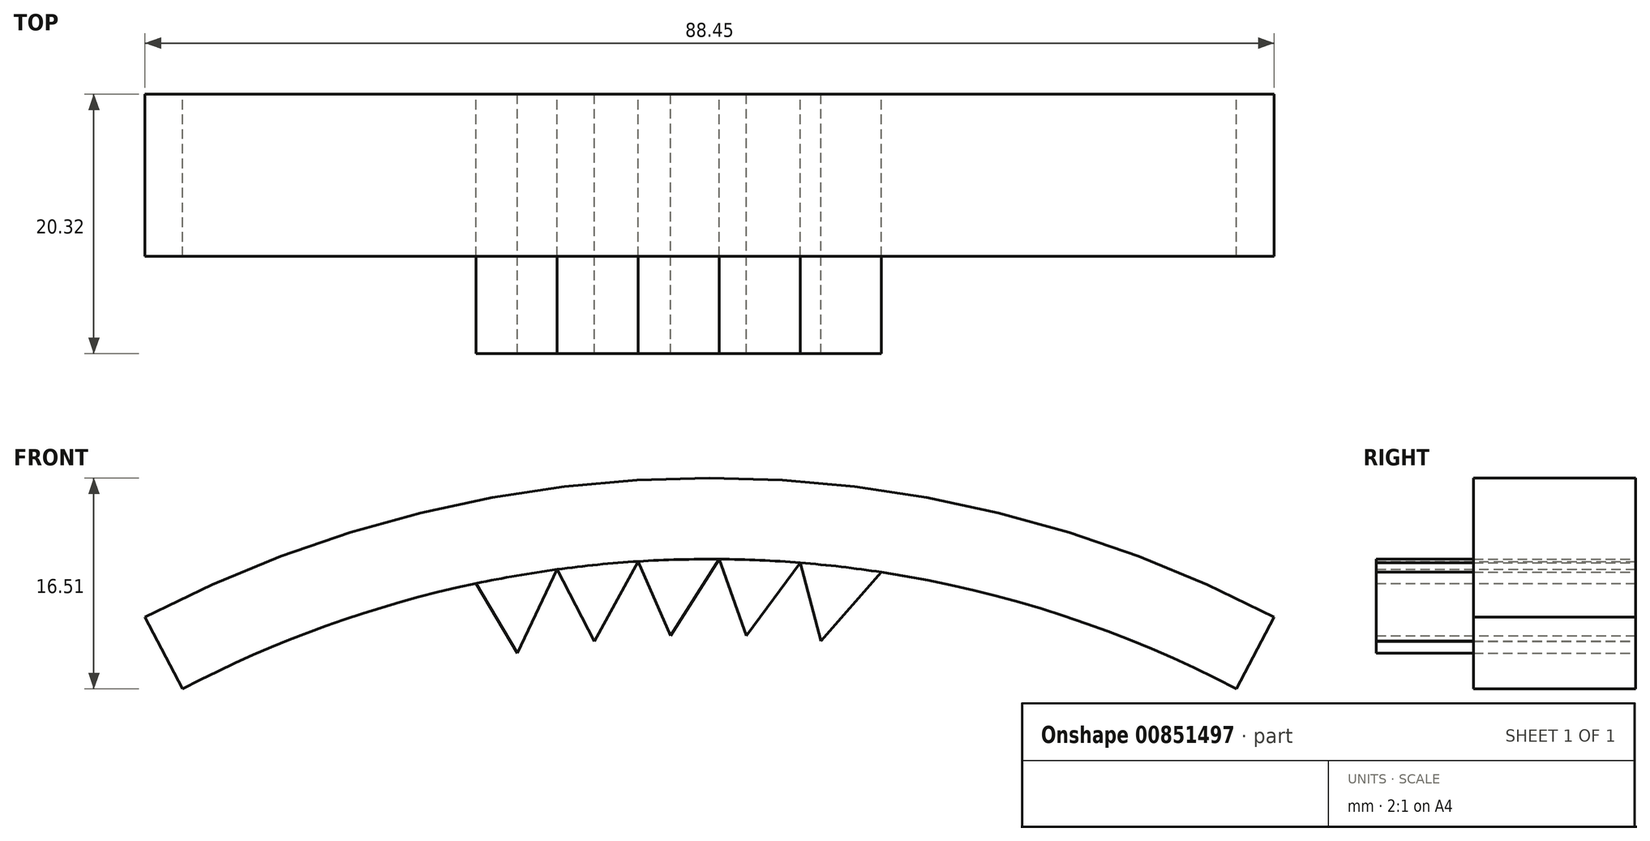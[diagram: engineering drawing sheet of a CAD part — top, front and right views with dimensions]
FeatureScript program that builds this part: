
annotation { "Feature Type Name" : "Feature", "Feature Type Description" : "" }
export const myFeature = defineFeature(function(context is Context, id is Id, definition is map)
    precondition{}
    {
        {
            var Q0;
            Q0=qCreatedBy(makeId("Front.planeOp"),FACE);
            var sketch = newSketch(context, id + "F0", { "sketchPlane" : qUnion([Q0])});
            skLineSegment(sketch, "E0", {"start": v(0, 0) * mm, "end": v(82.55, 0) * mm});
            skArc(sketch, "E1", {"start": v(82.55, 0) * mm, "mid": v(41.28, 10.16) * mm, "end": v(0, 0) * mm});
            skArc(sketch, "E2.0", {"start": v(85.5, 5.62) * mm, "mid": v(41.28, 16.51) * mm, "end": v(-2.95, 5.62) * mm});
            skLineSegment(sketch, "E3", {"start": v(0, 0) * mm, "end": v(-2.95, 5.62) * mm});
            skLineSegment(sketch, "E4", {"start": v(82.55, 0) * mm, "end": v(85.5, 5.62) * mm});
            skSolve(sketch);
        }
        {
            var Q0;
            Q0=makeQuery(id+"F0.imprint","IMPRINT",FACE,{"disambiguationData":[TD([[makeQuery(id+"F0.imprint","IMPRINT",EDGE,{"derivedFrom":sQuery(id+"F0.wireOp",EDGE,"E1")}),-1.0]])]});
            extrude(context, id + "F1", {"entities" : qUnion([Q0]), "depth" : 12.7 * mm, "offsetDistance" : 25.4 * mm});
        }
        {
            var Q0;
            Q0=makeQuery(id+"F1.opExtrude","CAP_FACE",FACE,{"disambiguationData":[OSD([sQuery(id+"F0.wireOp",EDGE,"E1"),sQuery(id+"F0.wireOp",EDGE,"E2.0"),sQuery(id+"F0.wireOp",EDGE,"E3"),sQuery(id+"F0.wireOp",EDGE,"E4")])],"isStart":false});
            var sketch = newSketch(context, id + "F2", { "sketchPlane" : qUnion([Q0])});
            skLineSegment(sketch, "E5", {"start": v(10.3, 4.59) * mm, "end": v(15.43, -0.34) * mm});
            skLineSegment(sketch, "E6", {"start": v(15.43, -0.34) * mm, "end": v(16.64, 6.68) * mm});
            skLineSegment(sketch, "E7", {"start": v(16.64, 6.68) * mm, "end": v(20.15, 1.39) * mm});
            skLineSegment(sketch, "E8", {"start": v(20.15, 1.39) * mm, "end": v(23, 8.26) * mm});
            skLineSegment(sketch, "E9", {"start": v(23, 8.26) * mm, "end": v(26.22, 2.8) * mm});
            skLineSegment(sketch, "E10", {"start": v(26.22, 2.8) * mm, "end": v(29.34, 9.36) * mm});
            skLineSegment(sketch, "E11", {"start": v(29.34, 9.36) * mm, "end": v(32.25, 3.71) * mm});
            skLineSegment(sketch, "E12", {"start": v(32.25, 3.71) * mm, "end": v(35.7, 9.98) * mm});
            skLineSegment(sketch, "E13", {"start": v(35.7, 9.98) * mm, "end": v(38.23, 4.16) * mm});
            skLineSegment(sketch, "E14", {"start": v(38.23, 4.16) * mm, "end": v(42.04, 10.16) * mm});
            skLineSegment(sketch, "E15", {"start": v(42.04, 10.16) * mm, "end": v(44.15, 4.17) * mm});
            skLineSegment(sketch, "E16", {"start": v(44.15, 4.17) * mm, "end": v(48.4, 9.87) * mm});
            skLineSegment(sketch, "E17", {"start": v(48.4, 9.87) * mm, "end": v(50.01, 3.73) * mm});
            skLineSegment(sketch, "E18", {"start": v(50.01, 3.73) * mm, "end": v(54.74, 9.13) * mm});
            skLineSegment(sketch, "E19", {"start": v(54.74, 9.13) * mm, "end": v(55.81, 2.88) * mm});
            skLineSegment(sketch, "E20", {"start": v(55.81, 2.88) * mm, "end": v(61.1, 7.92) * mm});
            skLineSegment(sketch, "E21", {"start": v(61.1, 7.92) * mm, "end": v(61.56, 1.6) * mm});
            skLineSegment(sketch, "E22", {"start": v(61.56, 1.6) * mm, "end": v(67.44, 6.22) * mm});
            skSolve(sketch);
        }
        {
            var Q0;
            {var subQ0=sQuery(id+"F2.wireOp",EDGE,"E9");Q0=makeQuery(id+"F2.imprint","IMPRINT",FACE,{"disambiguationData":[TD([[makeQuery(id+"F2.imprint","IMPRINT",EDGE,{"derivedFrom":subQ0}),1.0]])]});}
            var Q1;
            {var subQ0=sQuery(id+"F2.wireOp",EDGE,"E11");Q1=makeQuery(id+"F2.imprint","IMPRINT",FACE,{"disambiguationData":[TD([[makeQuery(id+"F2.imprint","IMPRINT",EDGE,{"derivedFrom":subQ0}),1.0]])]});}
            var Q2;
            {var subQ0=sQuery(id+"F2.wireOp",EDGE,"E13");Q2=makeQuery(id+"F2.imprint","IMPRINT",FACE,{"disambiguationData":[TD([[makeQuery(id+"F2.imprint","IMPRINT",EDGE,{"derivedFrom":subQ0}),1.0]])]});}
            var Q3;
            {var subQ0=sQuery(id+"F2.wireOp",EDGE,"E15");Q3=makeQuery(id+"F2.imprint","IMPRINT",FACE,{"disambiguationData":[TD([[makeQuery(id+"F2.imprint","IMPRINT",EDGE,{"derivedFrom":subQ0}),1.0]])]});}
            var Q4;
            {var subQ0=sQuery(id+"F2.wireOp",EDGE,"E17");Q4=makeQuery(id+"F2.imprint","IMPRINT",FACE,{"disambiguationData":[TD([[makeQuery(id+"F2.imprint","IMPRINT",EDGE,{"derivedFrom":subQ0}),1.0]])]});}
            extrude(context, id + "F3", {"entities" : qUnion([Q0, Q1, Q2, Q3, Q4]), "depth" : 7.62 * mm, "offsetDistance" : 25.4 * mm, "hasSecondDirection" : true, "secondDirectionOppositeDirection" : true, "secondDirectionDepth" : 12.7 * mm});
        }
    });
